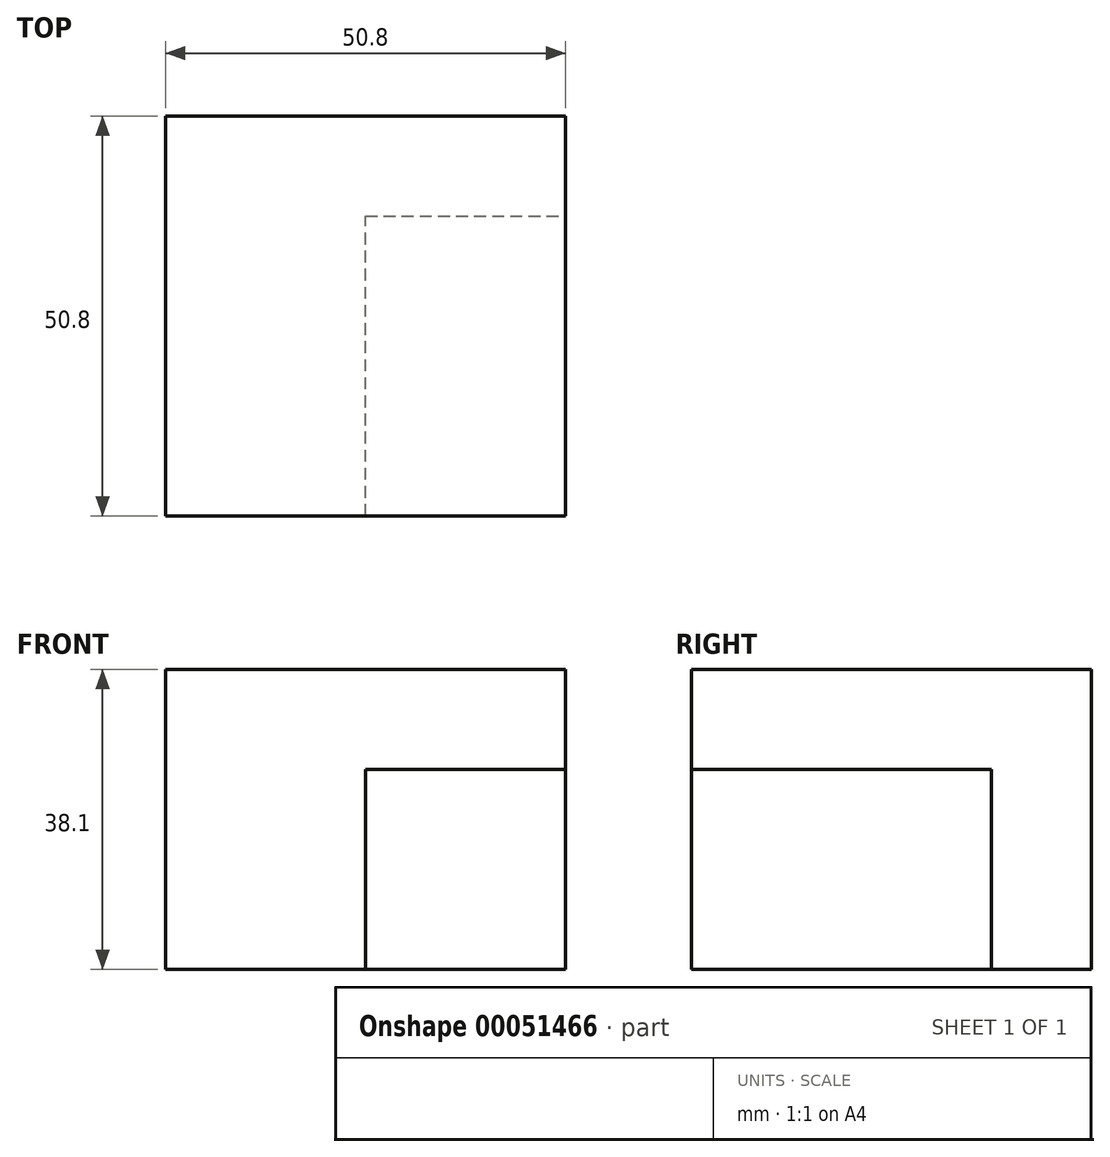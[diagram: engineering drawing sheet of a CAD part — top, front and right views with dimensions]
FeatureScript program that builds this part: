
annotation { "Feature Type Name" : "Feature", "Feature Type Description" : "" }
export const myFeature = defineFeature(function(context is Context, id is Id, definition is map)
    precondition{}
    {
        {
            var Q0;
            Q0=qCreatedBy(makeId("Top.planeOp"),FACE);
            var sketch = newSketch(context, id + "F0", { "sketchPlane" : qUnion([Q0])});
            skLineSegment(sketch, "E0.bottom", {"start": v(-28.82, 26.7) * mm, "end": v(21.98, 26.7) * mm});
            skLineSegment(sketch, "E0.top", {"start": v(-28.82, -24.1) * mm, "end": v(21.98, -24.1) * mm});
            skLineSegment(sketch, "E0.left", {"start": v(-28.82, 26.7) * mm, "end": v(-28.82, -24.1) * mm});
            skLineSegment(sketch, "E0.right", {"start": v(21.98, 26.7) * mm, "end": v(21.98, -24.1) * mm});
            skSolve(sketch);
        }
        {
            var Q0;
            Q0 = qSketchRegion(id + "F0", true);
            extrude(context, id + "F1", {"entities" : qUnion([Q0]), "depth" : 38.1 * mm});
        }
        {
            var Q0;
            Q0=qCreatedBy(makeId("Top.planeOp"),FACE);
            var sketch = newSketch(context, id + "F2", { "sketchPlane" : qUnion([Q0])});
            skLineSegment(sketch, "E1.0", {"start": v(-3.42, 14) * mm, "end": v(-3.42, -24.1) * mm, "construction": true});
            skLineSegment(sketch, "E2.0", {"start": v(-3.42, 14) * mm, "end": v(21.98, 14) * mm, "construction": true});
            skLineSegment(sketch, "E3", {"start": v(21.98, 14) * mm, "end": v(21.98, -24.1) * mm, "construction": true});
            skLineSegment(sketch, "E4", {"start": v(21.98, -24.1) * mm, "end": v(-3.42, -24.1) * mm, "construction": true});
            skLineSegment(sketch, "E5", {"start": v(-3.42, 14) * mm, "end": v(21.98, 14) * mm});
            skLineSegment(sketch, "E6", {"start": v(21.98, 14) * mm, "end": v(21.98, -24.1) * mm});
            skLineSegment(sketch, "E7", {"start": v(-3.42, -24.1) * mm, "end": v(21.98, -24.1) * mm});
            skLineSegment(sketch, "E8", {"start": v(-3.42, -24.1) * mm, "end": v(-3.42, 14) * mm});
            skSolve(sketch);
        }
        {
            var Q0;
            Q0 = qSketchRegion(id + "F2", true);
            extrude(context, id + "F3", {"entities" : qUnion([Q0]), "operationType" : NewBodyOperationType.REMOVE, "depth" : 25.4 * mm});
        }
    });
